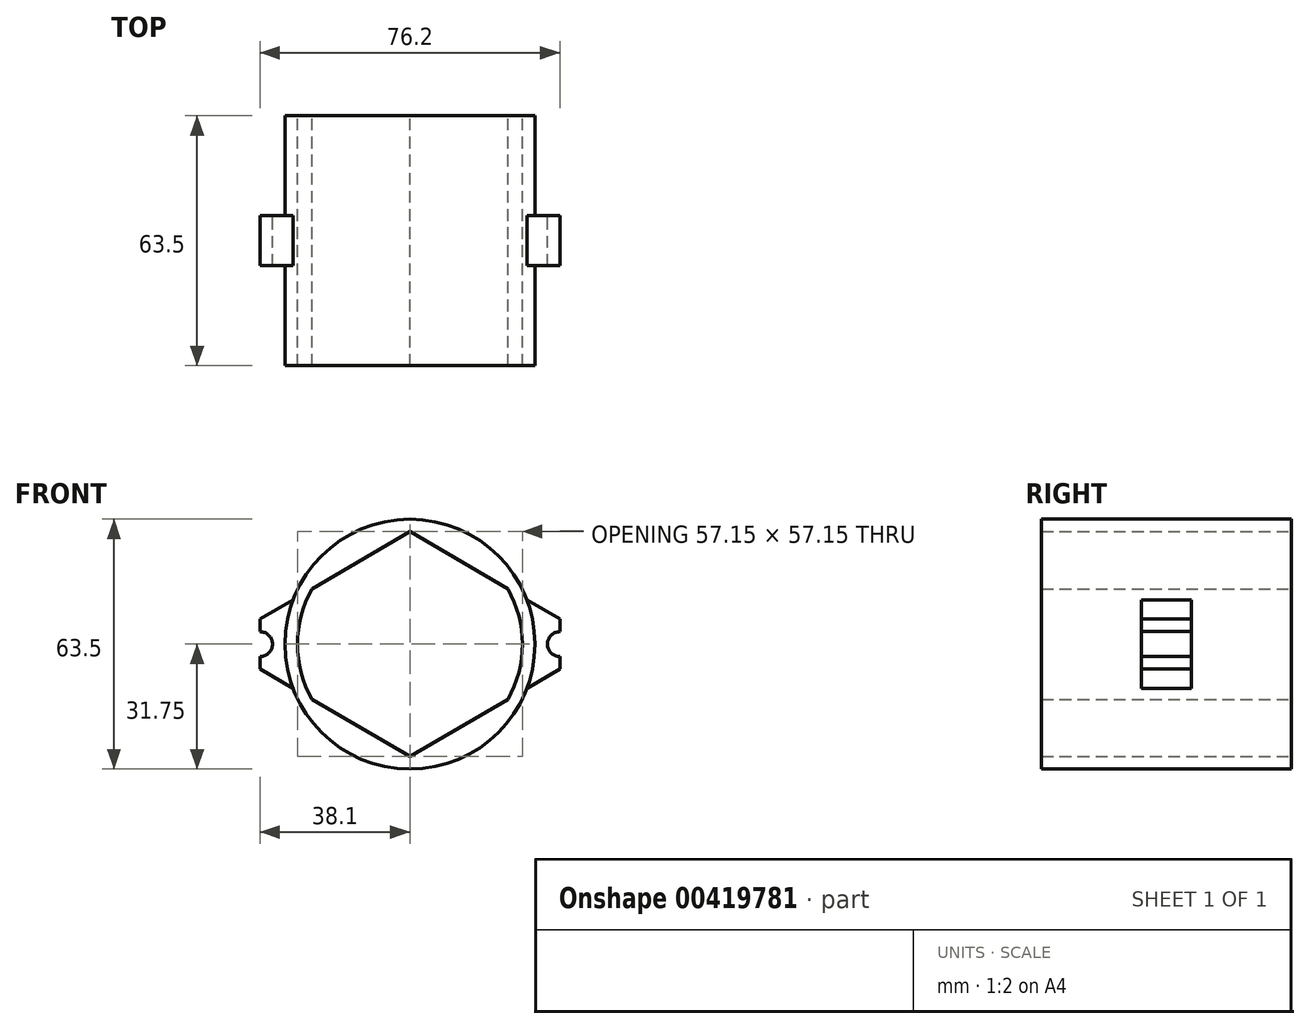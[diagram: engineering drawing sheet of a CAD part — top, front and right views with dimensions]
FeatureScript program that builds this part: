
annotation { "Feature Type Name" : "Feature", "Feature Type Description" : "" }
export const myFeature = defineFeature(function(context is Context, id is Id, definition is map)
    precondition{}
    {
        {
            var Q0;
            Q0=qCreatedBy(makeId("Front.planeOp"),FACE);
            var sketch = newSketch(context, id + "F0", { "sketchPlane" : qUnion([Q0])});
            skCircle(sketch, "E0", {"center": v(0, 0) * mm, "radius": 28.58 * mm});
            skCircle(sketch, "E1", {"center": v(0, 0) * mm, "radius": 31.75 * mm});
            skLineSegment(sketch, "E2", {"start": v(-31.75, 0) * mm, "end": v(-38.1, 0) * mm});
            skLineSegment(sketch, "E3", {"start": v(31.75, 0) * mm, "end": v(38.1, 0) * mm});
            skCircle(sketch, "E4", {"center": v(-38.1, 0) * mm, "radius": 6.35 * mm});
            skCircle(sketch, "E5", {"center": v(38.1, 0) * mm, "radius": 6.35 * mm});
            skLineSegment(sketch, "E6", {"start": v(-38.1, 0) * mm, "end": v(-38.1, 6.35) * mm});
            skLineSegment(sketch, "E7", {"start": v(-38.1, 6.35) * mm, "end": v(-38.1, 0) * mm});
            skLineSegment(sketch, "E8", {"start": v(-38.1, 0) * mm, "end": v(-38.1, -6.35) * mm});
            skLineSegment(sketch, "E9", {"start": v(38.1, 0) * mm, "end": v(38.1, 6.35) * mm});
            skLineSegment(sketch, "E10", {"start": v(38.1, 6.35) * mm, "end": v(38.1, 0) * mm});
            skLineSegment(sketch, "E11", {"start": v(38.1, 0) * mm, "end": v(38.1, -6.35) * mm});
            skLineSegment(sketch, "E12", {"start": v(0, 0) * mm, "end": v(0, 28.58) * mm});
            skLineSegment(sketch, "E13", {"start": v(0, 28.58) * mm, "end": v(0, 0) * mm});
            skLineSegment(sketch, "E14", {"start": v(0, -28.58) * mm, "end": v(0, 0) * mm});
            skLineSegment(sketch, "E15", {"start": v(-38.1, 6.35) * mm, "end": v(0, 28.58) * mm});
            skLineSegment(sketch, "E16", {"start": v(-38.1, -6.35) * mm, "end": v(0, -28.58) * mm});
            skLineSegment(sketch, "E17", {"start": v(0, 28.58) * mm, "end": v(38.1, 6.35) * mm});
            skLineSegment(sketch, "E18", {"start": v(0, -28.58) * mm, "end": v(38.1, -6.35) * mm});
            skSolve(sketch);
        }
        {
            var Q0;
            {var subQ1=sQuery(id+"F0.wireOp",EDGE,"E1");var subQ5=sQuery(id+"F0.wireOp",EDGE,"E17");var subQ6=makeQuery(id+"F0.imprint","INTERSECT",VERTEX,{"derivedFrom":[subQ1,subQ5]});Q0=makeQuery(id+"F0.imprint","IMPRINT",FACE,{"disambiguationData":[TD([[makeQuery(id+"F0.imprint","IMPRINT",EDGE,{"disambiguationData":[TD([[subQ6,-1.0]])],"derivedFrom":subQ1}),1.0]])]});}
            var Q1;
            {var subQ4=sQuery(id+"F0.wireOp",EDGE,"E15");var subQ6=sQuery(id+"F0.wireOp",EDGE,"E0");var subQ8=makeQuery(id+"F0.imprint","INTERSECT",VERTEX,{"derivedFrom":[subQ6,subQ4]});Q1=makeQuery(id+"F0.imprint","IMPRINT",FACE,{"disambiguationData":[TD([[makeQuery(id+"F0.imprint","IMPRINT",EDGE,{"disambiguationData":[TD([[subQ8,-1.0]])],"derivedFrom":subQ6}),-1.0]])]});}
            var Q2;
            {var subQ1=sQuery(id+"F0.wireOp",EDGE,"E13");Q2=makeQuery(id+"F0.imprint","IMPRINT",FACE,{"disambiguationData":[TD([[makeQuery(id+"F0.imprint","IMPRINT",EDGE,{"derivedFrom":subQ1}),-1.0]])]});}
            var Q3;
            {var subQ0=sQuery(id+"F0.wireOp",EDGE,"E15");var subQ1=sQuery(id+"F0.wireOp",EDGE,"E0");var subQ3=makeQuery(id+"F0.imprint","INTERSECT",VERTEX,{"derivedFrom":[subQ1,subQ0]});Q3=makeQuery(id+"F0.imprint","IMPRINT",FACE,{"disambiguationData":[TD([[makeQuery(id+"F0.imprint","IMPRINT",EDGE,{"disambiguationData":[TD([[subQ3,1.0]])],"derivedFrom":subQ1}),1.0]])]});}
            var Q4;
            {var subQ1=sQuery(id+"F0.wireOp",EDGE,"E13");Q4=makeQuery(id+"F0.imprint","IMPRINT",FACE,{"disambiguationData":[TD([[makeQuery(id+"F0.imprint","IMPRINT",EDGE,{"derivedFrom":subQ1}),1.0]])]});}
            var Q5;
            {var subQ0=sQuery(id+"F0.wireOp",EDGE,"E17");var subQ1=sQuery(id+"F0.wireOp",EDGE,"E0");var subQ3=makeQuery(id+"F0.imprint","INTERSECT",VERTEX,{"derivedFrom":[subQ1,subQ0]});Q5=makeQuery(id+"F0.imprint","IMPRINT",FACE,{"disambiguationData":[TD([[makeQuery(id+"F0.imprint","IMPRINT",EDGE,{"disambiguationData":[TD([[subQ3,-1.0]])],"derivedFrom":subQ1}),1.0]])]});}
            var Q6;
            {var subQ0=sQuery(id+"F0.wireOp",EDGE,"E17");var subQ3=sQuery(id+"F0.wireOp",EDGE,"E0");var subQ4=makeQuery(id+"F0.imprint","INTERSECT",VERTEX,{"derivedFrom":[subQ3,subQ0]});Q6=makeQuery(id+"F0.imprint","IMPRINT",FACE,{"disambiguationData":[TD([[makeQuery(id+"F0.imprint","IMPRINT",EDGE,{"disambiguationData":[TD([[subQ4,1.0]])],"derivedFrom":subQ3}),-1.0]])]});}
            var Q7;
            {var subQ0=sQuery(id+"F0.wireOp",EDGE,"E16");var subQ1=sQuery(id+"F0.wireOp",EDGE,"E1");var subQ2=makeQuery(id+"F0.imprint","INTERSECT",VERTEX,{"derivedFrom":[subQ1,subQ0]});Q7=makeQuery(id+"F0.imprint","IMPRINT",FACE,{"disambiguationData":[TD([[makeQuery(id+"F0.imprint","IMPRINT",EDGE,{"disambiguationData":[TD([[subQ2,-1.0]])],"derivedFrom":subQ1}),1.0]])]});}
            var Q8;
            {var subQ0=sQuery(id+"F0.wireOp",EDGE,"E18");var subQ1=sQuery(id+"F0.wireOp",EDGE,"E0");var subQ3=makeQuery(id+"F0.imprint","INTERSECT",VERTEX,{"derivedFrom":[subQ1,subQ0]});Q8=makeQuery(id+"F0.imprint","IMPRINT",FACE,{"disambiguationData":[TD([[makeQuery(id+"F0.imprint","IMPRINT",EDGE,{"disambiguationData":[TD([[subQ3,1.0]])],"derivedFrom":subQ1}),1.0]])]});}
            var Q9;
            {var subQ0=sQuery(id+"F0.wireOp",EDGE,"E16");var subQ1=sQuery(id+"F0.wireOp",EDGE,"E0");var subQ3=makeQuery(id+"F0.imprint","INTERSECT",VERTEX,{"derivedFrom":[subQ1,subQ0]});Q9=makeQuery(id+"F0.imprint","IMPRINT",FACE,{"disambiguationData":[TD([[makeQuery(id+"F0.imprint","IMPRINT",EDGE,{"disambiguationData":[TD([[subQ3,-1.0]])],"derivedFrom":subQ1}),1.0]])]});}
            extrude(context, id + "F1", {"entities" : qUnion([Q0, Q1, Q2, Q3, Q4, Q5, Q6, Q7, Q8, Q9]), "endBound" : BoundingType.SYMMETRIC, "depth" : 63.5 * mm, "offsetDistance" : 25.4 * mm});
        }
        {
            var Q0;
            {var subQ1=sQuery(id+"F0.wireOp",EDGE,"E1");var subQ3=sQuery(id+"F0.wireOp",EDGE,"E17");var subQ4=makeQuery(id+"F0.imprint","INTERSECT",VERTEX,{"derivedFrom":[subQ1,subQ3]});Q0=makeQuery(id+"F0.imprint","IMPRINT",FACE,{"disambiguationData":[TD([[makeQuery(id+"F0.imprint","IMPRINT",EDGE,{"disambiguationData":[TD([[subQ4,1.0]])],"derivedFrom":subQ1}),-1.0]])]});}
            var Q1;
            {var subQ0=sQuery(id+"F0.wireOp",EDGE,"E3");Q1=makeQuery(id+"F0.imprint","IMPRINT",FACE,{"disambiguationData":[TD([[makeQuery(id+"F0.imprint","IMPRINT",EDGE,{"derivedFrom":subQ0}),1.0]])]});}
            var Q2;
            {var subQ0=sQuery(id+"F0.wireOp",EDGE,"E10");Q2=makeQuery(id+"F0.imprint","IMPRINT",FACE,{"disambiguationData":[TD([[makeQuery(id+"F0.imprint","IMPRINT",EDGE,{"derivedFrom":subQ0}),1.0]])]});}
            var Q3;
            {var subQ0=sQuery(id+"F0.wireOp",EDGE,"E3");Q3=makeQuery(id+"F0.imprint","IMPRINT",FACE,{"disambiguationData":[TD([[makeQuery(id+"F0.imprint","IMPRINT",EDGE,{"derivedFrom":subQ0}),-1.0]])]});}
            var Q4;
            {var subQ1=sQuery(id+"F0.wireOp",EDGE,"E1");var subQ3=sQuery(id+"F0.wireOp",EDGE,"E18");var subQ4=makeQuery(id+"F0.imprint","INTERSECT",VERTEX,{"derivedFrom":[subQ1,subQ3]});Q4=makeQuery(id+"F0.imprint","IMPRINT",FACE,{"disambiguationData":[TD([[makeQuery(id+"F0.imprint","IMPRINT",EDGE,{"disambiguationData":[TD([[subQ4,-1.0]])],"derivedFrom":subQ1}),-1.0]])]});}
            var Q5;
            {var subQ0=sQuery(id+"F0.wireOp",EDGE,"E7");Q5=makeQuery(id+"F0.imprint","IMPRINT",FACE,{"disambiguationData":[TD([[makeQuery(id+"F0.imprint","IMPRINT",EDGE,{"derivedFrom":subQ0}),-1.0]])]});}
            var Q6;
            {var subQ0=sQuery(id+"F0.wireOp",EDGE,"E2");Q6=makeQuery(id+"F0.imprint","IMPRINT",FACE,{"disambiguationData":[TD([[makeQuery(id+"F0.imprint","IMPRINT",EDGE,{"derivedFrom":subQ0}),-1.0]])]});}
            var Q7;
            {var subQ0=sQuery(id+"F0.wireOp",EDGE,"E2");Q7=makeQuery(id+"F0.imprint","IMPRINT",FACE,{"disambiguationData":[TD([[makeQuery(id+"F0.imprint","IMPRINT",EDGE,{"derivedFrom":subQ0}),1.0]])]});}
            var Q8;
            {var subQ1=sQuery(id+"F0.wireOp",EDGE,"E1");var subQ3=sQuery(id+"F0.wireOp",EDGE,"E15");var subQ4=makeQuery(id+"F0.imprint","INTERSECT",VERTEX,{"derivedFrom":[subQ1,subQ3]});Q8=makeQuery(id+"F0.imprint","IMPRINT",FACE,{"disambiguationData":[TD([[makeQuery(id+"F0.imprint","IMPRINT",EDGE,{"disambiguationData":[TD([[subQ4,-1.0]])],"derivedFrom":subQ1}),-1.0]])]});}
            var Q9;
            {var subQ1=sQuery(id+"F0.wireOp",EDGE,"E1");var subQ3=sQuery(id+"F0.wireOp",EDGE,"E16");var subQ4=makeQuery(id+"F0.imprint","INTERSECT",VERTEX,{"derivedFrom":[subQ1,subQ3]});Q9=makeQuery(id+"F0.imprint","IMPRINT",FACE,{"disambiguationData":[TD([[makeQuery(id+"F0.imprint","IMPRINT",EDGE,{"disambiguationData":[TD([[subQ4,1.0]])],"derivedFrom":subQ1}),-1.0]])]});}
            extrude(context, id + "F2", {"entities" : qUnion([Q0, Q1, Q2, Q3, Q4, Q5, Q6, Q7, Q8, Q9]), "operationType" : NewBodyOperationType.ADD, "endBound" : BoundingType.SYMMETRIC, "depth" : 12.7 * mm, "offsetDistance" : 25.4 * mm});
        }
        {
            var Q0;
            Q0=makeQuery(id+"F2.opExtrude","CAP_FACE",FACE,{"disambiguationData":[OSD([sQuery(id+"F0.wireOp",EDGE,"E1"),sQuery(id+"F0.wireOp",EDGE,"E5"),sQuery(id+"F0.wireOp",EDGE,"E17"),sQuery(id+"F0.wireOp",EDGE,"E18")])],"isStart":true});
            var sketch = newSketch(context, id + "F3", { "sketchPlane" : qUnion([Q0])});
            skPoint(sketch, "E19", {"position": v(-38.1, 0) * mm});
            skSolve(sketch);
        }
        {
            var Q0;
            Q0=makeQuery(id+"F2.opExtrude","CAP_FACE",FACE,{"disambiguationData":[OSD([sQuery(id+"F0.wireOp",EDGE,"E1"),sQuery(id+"F0.wireOp",EDGE,"E4"),sQuery(id+"F0.wireOp",EDGE,"E15"),sQuery(id+"F0.wireOp",EDGE,"E16")])],"isStart":true});
            var sketch = newSketch(context, id + "F4", { "sketchPlane" : qUnion([Q0])});
            skPoint(sketch, "E20", {"position": v(38.1, 0) * mm});
            skSolve(sketch);
        }
        {
            var Q0;
            Q0=sQuery(id+"F3.wireOp",VERTEX,"E19");
            var Q1;
            Q1=sQuery(id+"F4.wireOp",VERTEX,"E20");
            var Q2;
            Q2=makeQuery(id+"F1.opExtrude","SWEPT_BODY",BODY,{"disambiguationData":[OSD([sQuery(id+"F0.wireOp",EDGE,"E1")])]});
            hole(context, id + "F5", {"style" : HoleStyle.SIMPLE, "endStyle" : HoleEndStyle.THROUGH, "holeDiameter" : 6.35 * mm, "majorDiameter" : 6.35 * mm, "isTappedThrough" : true, "tappedDepth" : 12.7 * mm, "tapClearance" : 3, "locations" : qUnion([Q0, Q1]), "scope" : qUnion([Q2])});
        }
    });
